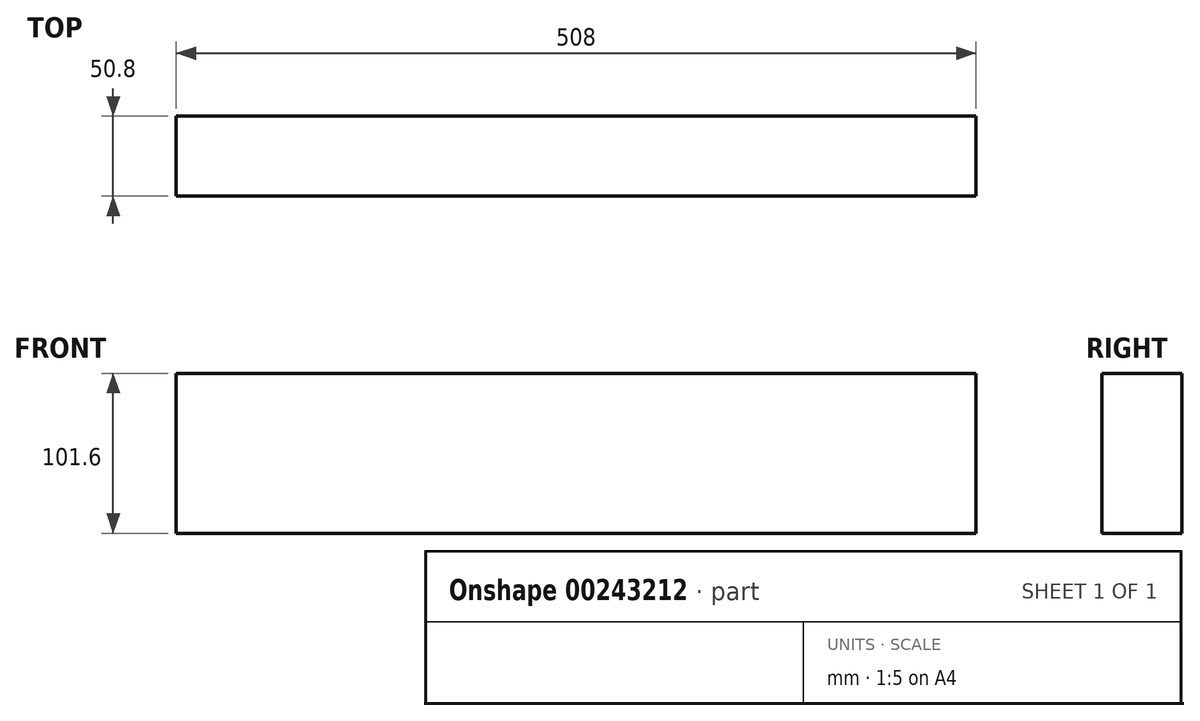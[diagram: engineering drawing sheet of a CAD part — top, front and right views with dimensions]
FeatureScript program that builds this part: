
annotation { "Feature Type Name" : "Feature", "Feature Type Description" : "" }
export const myFeature = defineFeature(function(context is Context, id is Id, definition is map)
    precondition{}
    {
        {
            var Q0;
            Q0=qCreatedBy(makeId("Right.planeOp"),FACE);
            var sketch = newSketch(context, id + "F0", { "sketchPlane" : qUnion([Q0])});
            skLineSegment(sketch, "E0.bottom", {"start": v(25.4, -50.8) * mm, "end": v(-25.4, -50.8) * mm});
            skLineSegment(sketch, "E0.top", {"start": v(25.4, 50.8) * mm, "end": v(-25.4, 50.8) * mm});
            skLineSegment(sketch, "E0.left", {"start": v(25.4, -50.8) * mm, "end": v(25.4, 50.8) * mm});
            skLineSegment(sketch, "E0.right", {"start": v(-25.4, -50.8) * mm, "end": v(-25.4, 50.8) * mm});
            skPoint(sketch, "E0.middle", {"position": v(0, 0) * mm});
            skSolve(sketch);
        }
        {
            var Q0;
            Q0 = qSketchRegion(id + "F0", true);
            extrude(context, id + "F1", {"entities" : qUnion([Q0]), "depth" : 508 * mm});
        }
    });
